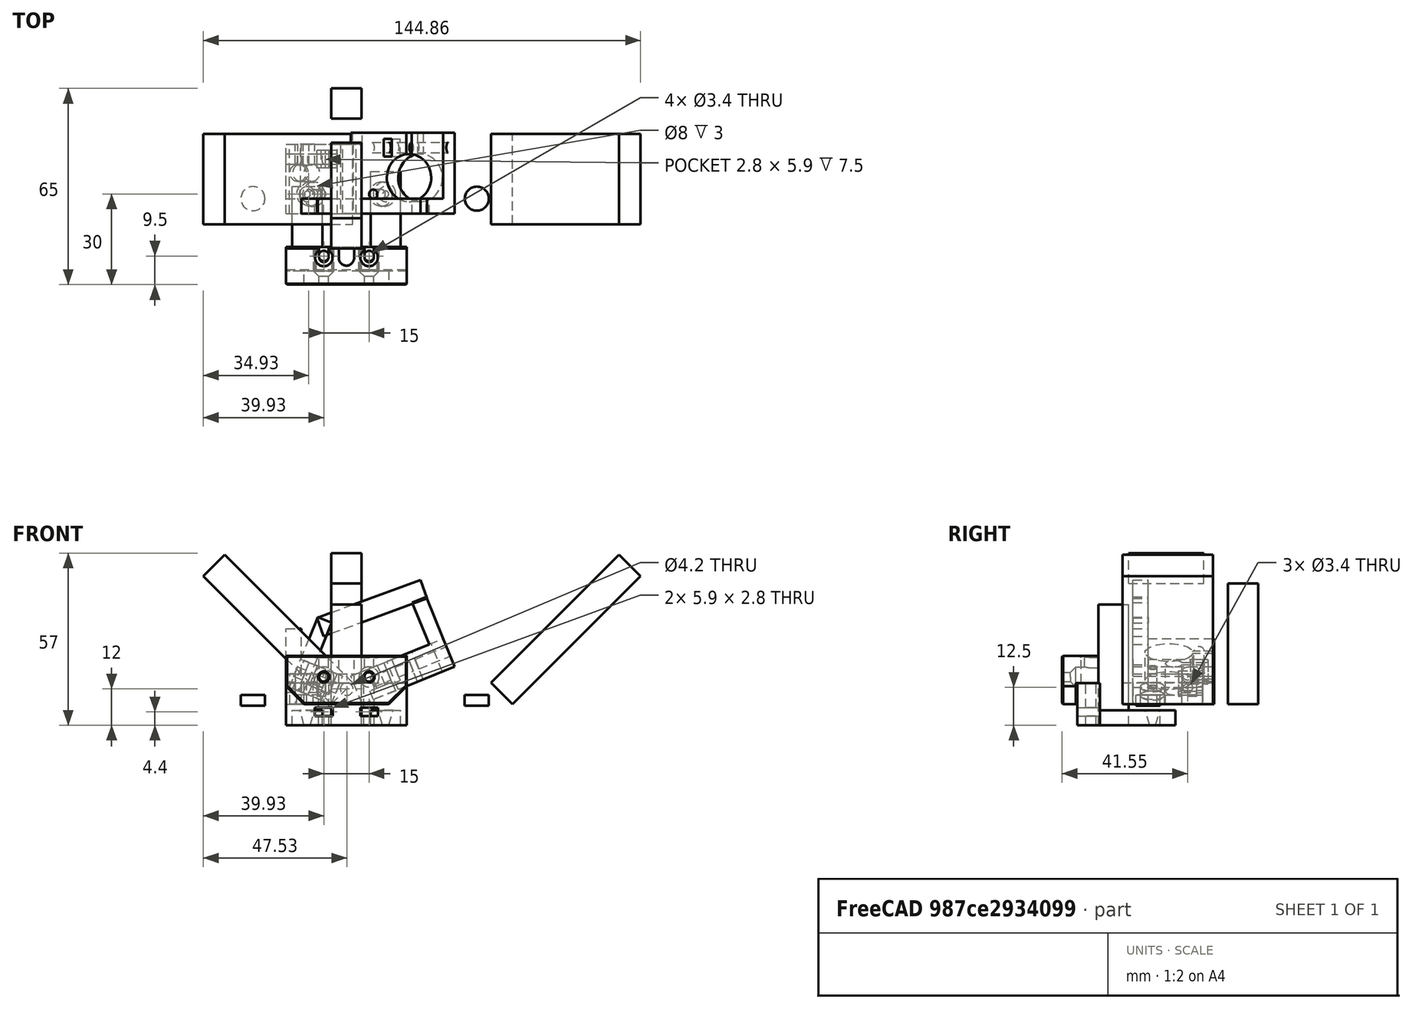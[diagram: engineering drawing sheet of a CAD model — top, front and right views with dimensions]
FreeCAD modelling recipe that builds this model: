
FCSTD DOCUMENT  (FreeCAD 0.14R3702 (Git))
Label: rocking-head
License: CC-BY 3.0
LicenseURL: http://creativecommons.org/licenses/by/3.0/
objects: Part::Box×20, Part::Fuse×12, Part::Cylinder×10, Part::Cut×9, Part::Mirroring×3, App::DocumentObjectGroup×2, Part::Cone×2, Part::Feature×1
note: 57 computed .brp shape members not serialized (recipe doc carries the construction recipe); baked Part::Feature solids carry a one-line shape summary decoded from their .brp

FEATURE [Part::Box] Box  label="Joining base"
  Height = 10
  Length = 10.2
  Placement = pos=(0,3.5,0) rot=(0,0,1;0rad)
  Width = 23
FEATURE [Part::Box] Box001  label="Cube001"
  Height = 10
  Length = 60
  Placement = pos=(60,0,0) rot=(0,-1,0;0.785398rad)
  Width = 30
FEATURE [Part::Box] Box003  label="Cube003"
  Height = 10
  Length = 60
  Placement = pos=(0,0,0) rot=(0,-1,0;0.785398rad)
  Width = 30
FEATURE [Part::Mirroring] Part__Mirroring  label="Cube003 (Mirror #1)"
  Base = (0,0,0)
  Normal = (1,0,0)
  Source = -> Box003
FEATURE [Part::Box] Box004  label="Cube004"
  Height = 10
  Length = 10
  Placement = pos=(20,-6,20) rot=(0,0,1;0rad)
  Width = 42
FEATURE [Part::Box] Box005  label="Cube005"
  Height = 20
  Length = 10
  Placement = pos=(20,-6,0) rot=(0,0,1;0rad)
  Width = 10
FEATURE [Part::Box] Box008  label="Watercooled original cube"
  Height = 10
  Length = 33
  Placement = pos=(10.2,3.5,0) rot=(0,0,1;0rad)
  Width = 26.85
FEATURE [Part::Fuse] Fusion001
  Tool = -> Box004
FEATURE [Part::Fuse] Fusion002  label="nut-trap004"
  Placement = pos=(17,5,10) rot=(-1,0,0;1.5708rad)
  Tool = -> Box005
FEATURE [Part::Fuse] Fusion
  Base = -> Fusion002
  Placement = pos=(82,30,0) rot=(0,0,1;3.14159rad)
  Tool = -> Fusion001
FEATURE [Part::Mirroring] Part__Mirroring001  label="Watercooled Holes fusion"
  Base = (0,0,0)
  Normal = (1,0,0)
  Placement = pos=(43,90.4,0) rot=(0,0,1;1.5708rad)
  Source = -> Fusion
FEATURE [Part::Fuse] Fusion004
FEATURE [Part::Box] Box009  label="Cube007"
  Height = 13
  Length = 10
  Placement = pos=(-22,17,-1) rot=(0,0,1;0rad)
  Width = 2
FEATURE [Part::Fuse] Fusion003
  Base = -> Box009
  Placement = pos=(-10.55,0,0) rot=(0,0,1;0rad)
  Tool = -> Fusion004
FEATURE [Part::Box] Box010  label="Quick-set original cube"
  Height = 10
  Length = 15
  Placement = pos=(-15,3.5,0) rot=(0,0,1;0rad)
  Width = 23
FEATURE [Part::Cylinder] Cylinder
  Angle = 360
  Height = 25
  Placement = pos=(5.1,27.5,5) rot=(1,0,0;1.5708rad)
  Radius = 2.1
FEATURE [Part::Cut] Cut002  label="Joining base with hole"
  Base = -> Box
  Tool = -> Cylinder
FEATURE [Part::Mirroring] Part__Mirroring002  label="Quick-set holes fusion"
  Base = (0,0,0)
  Normal = (0,1,0)
  Placement = pos=(7,-5.5,0) rot=(0,0,-1;1.5708rad)
  Source = -> Fusion003
FEATURE [Part::Cylinder] Cylinder001  label="Magnet (Quick-set)"
  Angle = 360
  Height = 3.5
  Placement = pos=(-7.5,10,-0.5) rot=(0,0,1;0rad)
  Radius = 4
FEATURE [Part::Cylinder] Cylinder002  label="Magnet (watercooled)"
  Angle = 360
  Height = 3.5
  Placement = pos=(18.2,10,-0.5) rot=(0,0,1;0rad)
  Radius = 4
FEATURE [Part::Box] Box011  label="Tipping Flag (Quick-set)"
  Height = 15
  Length = 5
  Placement = pos=(-15,3.5,10) rot=(0,0,1;0rad)
  Width = 5
FEATURE [Part::Box] Box012  label="Cube to cut 22 angle so fits with Quick-set"
  Height = 10
  Length = 10.2
  Placement = pos=(-9.45728,3.5,3.82099) rot=(0,1,0;0.383972rad)
  Width = 23
FEATURE [Part::Cylinder] Cylinder003  label="Magnet end (Quick-set)"
  Angle = 360
  Height = 3.5
  Placement = pos=(-26,8.5,-0.5) rot=(0,0,1;0rad)
  Radius = 4
FEATURE [Part::Cylinder] Cylinder004  label="Magnet end (watercooled)"
  Angle = 360
  Height = 3.5
  Placement = pos=(48.2,8.5,-0.5) rot=(0,0,1;0rad)
  Radius = 4
FEATURE [Part::Cut] Cut008
  Base = -> Box010
  Tool = -> Part__Mirroring002
FEATURE [Part::Cut] Cut009  label="Quick-set mount 1 magnet"
  Base = -> Cut008
  Tool = -> Cylinder001
FEATURE [Part::Cylinder] Cylinder005  label="Punch hole (Quick-set magnet)"
  Angle = 360
  Height = 10
  Placement = pos=(-7.5,10,0) rot=(0,0,1;0rad)
  Radius = 1.5
FEATURE [Part::Cut] Cut
  Base = -> Box008
  Tool = -> Part__Mirroring001
FEATURE [Part::Cylinder] Cylinder006  label="Punch hole (watercooled magnet)"
  Angle = 360
  Height = 10
  Placement = pos=(18.2,10,0) rot=(0,0,1;0rad)
  Radius = 1.5
FEATURE [Part::Cut] Cut011  label="Watercooled mount 1 magnet"
  Base = -> Cut
  Tool = -> Cylinder002
FEATURE [Part::Box] Box013  label="Tipping Flag (watercooled)"
  Height = 15
  Length = 5
  Placement = pos=(38.2,3.5,10) rot=(0,0,1;0rad)
  Width = 5
FEATURE [Part::Fuse] Fusion006  label="Watercooled mount inc magnet and flag"
  Base = -> Cut011
  Tool = -> Box013
FEATURE [Part::Cut] Cut012  label="Watercooled mount inc magnet plus punch and flag"
  Base = -> Fusion006
  Placement = pos=(0.742725,0,-3.82099) rot=(0,-1,0;0.383972rad)
  Tool = -> Cylinder006
FEATURE [Part::Cylinder] Cylinder007  label="Punch hole (Quick-set magnet)001"
  Angle = 360
  Height = 10
  Placement = pos=(-7.5,10,0) rot=(0,0,1;0rad)
  Radius = 1.5
FEATURE [Part::Fuse] Fusion007  label="Quick-set mount inc magnet and flag001"
  Base = -> Box011
  Tool = -> Cut009
FEATURE [App::DocumentObjectGroup] Group001  label="Deleted groups"
  Group = -> [Fusion007,Cylinder007]
FEATURE [App::DocumentObjectGroup] Group  label="Working"
  Group = -> [Box001,Part__Mirroring,Cylinder003,Cylinder004,Group001]
FEATURE [Part::Cut] Cut013  label="Joining base with cut and hole"
  Base = -> Cut002
  Tool = -> Box012
FEATURE [Part::Fuse] Fusion008
  Base = -> Cut012
  Tool = -> Cut013
FEATURE [Part::Fuse] Fusion005  label="Quick-set mount inc magnet and flag"
  Base = -> Box011
  Tool = -> Cut009
FEATURE [Part::Cut] Cut010  label="Quick-set mount inc magnet plus punch and flag"
  Base = -> Fusion005
  Placement = pos=(0,0,0) rot=(0,1,0;0.383972rad)
  Tool = -> Cylinder005
FEATURE [Part::Box] Box014  label="Cube"
  Height = 6.5
  Length = 36.5
  Placement = pos=(-2.55,3.5,22.5) rot=(0,-1,0;0.349066rad)
  Width = 5
FEATURE [Part::Box] Box015  label="Cube002"
  Height = 40
  Length = 10
  Placement = pos=(0,35,0) rot=(0,0,1;0rad)
  Width = 10
FEATURE [Part::Box] Box016  label="Cube008"
  Height = 40
  Length = 10
  Placement = pos=(0,-8,-7) rot=(0,0,1;0rad)
  Width = 10
FEATURE [Part::Box] Box017  label="Cube009"
  Height = 10
  Length = 10
  Placement = pos=(0,2,40) rot=(0,0,1;0rad)
  Width = 25
FEATURE [Part::Feature] Part__Feature  label="501 Nozzle Mount"
  Placement = pos=(5,-20,0) rot=(0,0.707107,0.707107;3.14159rad)
  shape: bbox 40 x 12 x 16 mm, 56 faces (baked)
FEATURE [Part::Box] Box018  label="Cube010"
  Height = 2.8
  Length = 5.9
  Placement = pos=(-2.95,-2.5,4) rot=(0,0,1;0rad)
  Width = 10
FEATURE [Part::Cylinder] Cylinder008
  Angle = 360
  Height = 29
  Placement = pos=(0,4.5,-2) rot=(0,0,1;0rad)
  Radius = 1.7
FEATURE [Part::Fuse] Fusion010  label="Nozzle mount nut-trap002"
  Base = -> Cylinder008
  Placement = pos=(7.5,0,0) rot=(0,0,1;0rad)
  Tool = -> Box018
FEATURE [Part::Box] Box019  label="Cube011"
  Height = 2.8
  Length = 5.9
  Placement = pos=(-2.95,-2.5,4) rot=(0,0,1;0rad)
  Width = 10
FEATURE [Part::Cylinder] Cylinder009
  Angle = 360
  Height = 29
  Placement = pos=(0,4.5,-2) rot=(0,0,1;0rad)
  Radius = 1.7
FEATURE [Part::Fuse] Fusion011  label="nut-trap001"
  Base = -> Cylinder009
  Placement = pos=(-7.5,0,0) rot=(0,0,1;0rad)
  Tool = -> Box019
FEATURE [Part::Fuse] Fusion012  label="Nut trap holes(to attach to nozzle mount"
  Base = -> Fusion010
  Placement = pos=(5,-15,-8) rot=(0,0,1;0rad)
  Tool = -> Fusion011
FEATURE [Part::Box] Box020  label="Mount cube"
  Height = 14
  Length = 40
  Placement = pos=(-15,-15,-7) rot=(0,0,1;0rad)
  Width = 7.5
FEATURE [Part::Cut] Cut014  label="Mount with nut trap"
  Base = -> Box020
  Tool = -> Fusion012
FEATURE [Part::Box] Box021  label="Cube012"
  Height = 5
  Length = 10
  Placement = pos=(-13,-7.5,-7) rot=(0,0,1;0rad)
  Width = 20
FEATURE [Part::Box] Box022  label="Cube013"
  Height = 5
  Length = 10
  Placement = pos=(13,-7.5,-7) rot=(0,0,1;0rad)
  Width = 25
FEATURE [Part::Cone] Cone
  Angle = 360
  Height = 5
  Placement = pos=(18,10,-7) rot=(0,0,1;0rad)
  Radius1 = 1
  Radius2 = 2.5
FEATURE [Part::Cone] Cone001
  Angle = 360
  Height = 5
  Placement = pos=(-8,10,-7) rot=(0,0,1;0rad)
  Radius1 = 1
  Radius2 = 2.5
